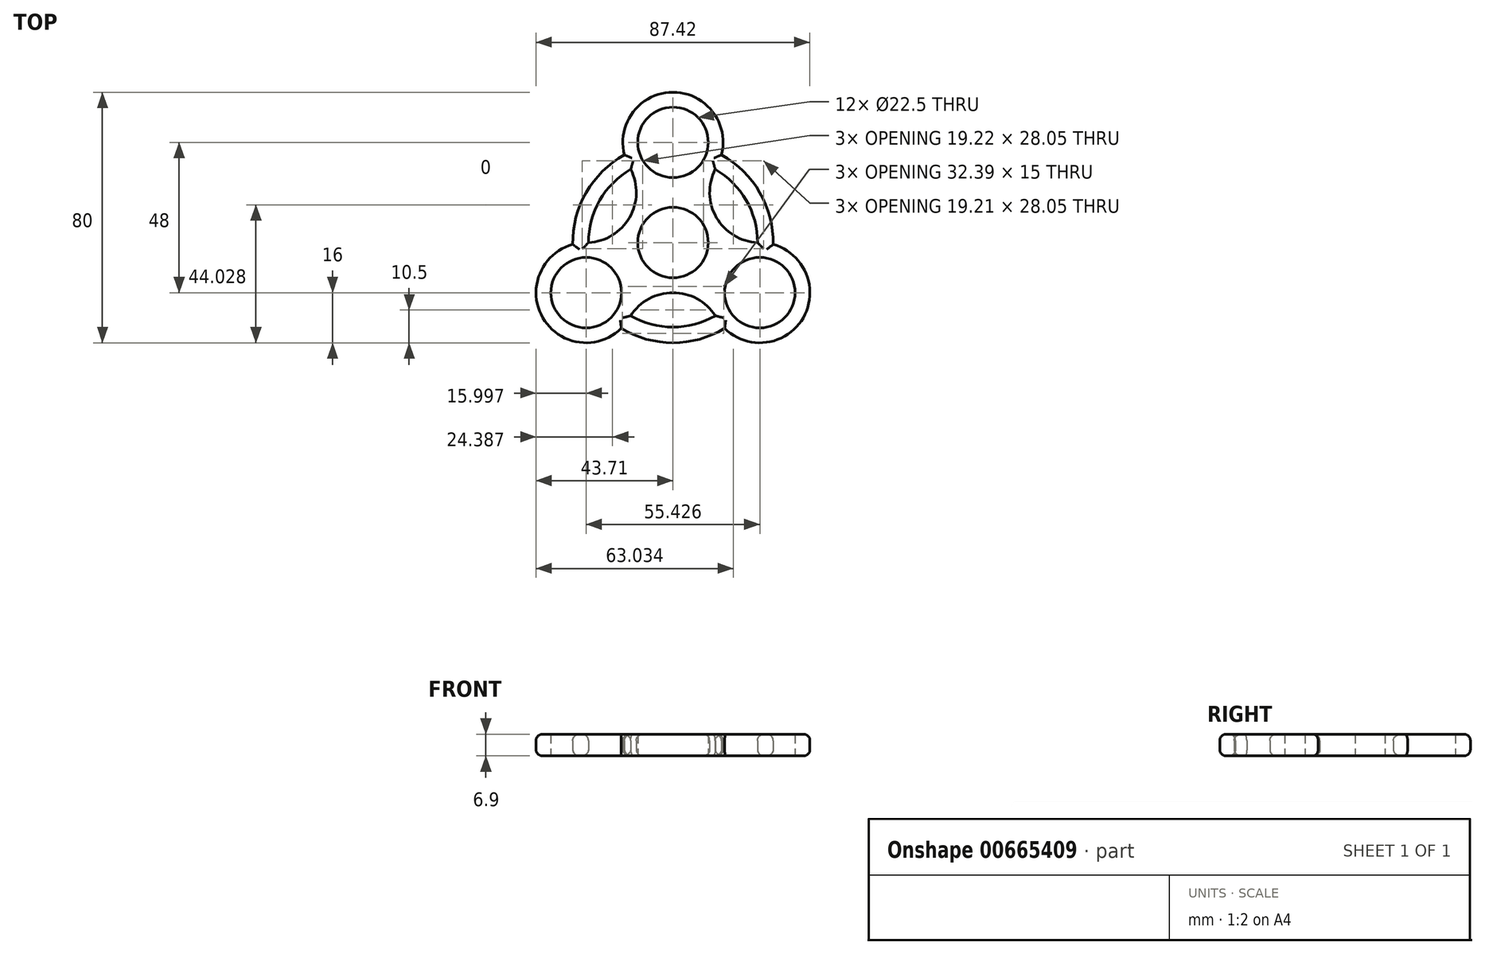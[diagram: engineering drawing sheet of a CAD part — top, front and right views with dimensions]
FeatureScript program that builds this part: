
annotation { "Feature Type Name" : "Feature", "Feature Type Description" : "" }
export const myFeature = defineFeature(function(context is Context, id is Id, definition is map)
    precondition{}
    {
        {
            var Q0;
            Q0=qCreatedBy(makeId("Top.planeOp"),FACE);
            var sketch = newSketch(context, id + "F0", { "sketchPlane" : qUnion([Q0])});
            skCircle(sketch, "E0.cCircle", {"center": v(0, 0) * mm, "radius": 32 * mm});
            skLineSegment(sketch, "E0.0", {"start": v(55.43, -32) * mm, "end": v(-55.43, -32) * mm, "construction": true});
            skLineSegment(sketch, "E0.1", {"start": v(-55.43, -32) * mm, "end": v(0, 64) * mm, "construction": true});
            skLineSegment(sketch, "E0.2", {"start": v(0, 64) * mm, "end": v(55.43, -32) * mm, "construction": true});
            skPoint(sketch, "E0.0.midPoint", {"position": v(0, -32) * mm});
            skCircle(sketch, "E1.cCircle", {"center": v(0, 0) * mm, "radius": 27 * mm});
            skLineSegment(sketch, "E1.0", {"start": v(46.77, -27) * mm, "end": v(-46.77, -27) * mm, "construction": true});
            skLineSegment(sketch, "E1.1", {"start": v(-46.77, -27) * mm, "end": v(0, 54) * mm, "construction": true});
            skLineSegment(sketch, "E1.2", {"start": v(0, 54) * mm, "end": v(46.77, -27) * mm, "construction": true});
            skPoint(sketch, "E1.0.midPoint", {"position": v(0, -27) * mm});
            skCircle(sketch, "E2.cCircle", {"center": v(0, 0) * mm, "radius": 16 * mm, "construction": true});
            skLineSegment(sketch, "E2.0", {"start": v(27.71, -16) * mm, "end": v(-27.71, -16) * mm, "construction": true});
            skLineSegment(sketch, "E2.1", {"start": v(-27.71, -16) * mm, "end": v(0, 32) * mm, "construction": true});
            skLineSegment(sketch, "E2.2", {"start": v(0, 32) * mm, "end": v(27.71, -16) * mm, "construction": true});
            skPoint(sketch, "E2.0.midPoint", {"position": v(0, -16) * mm});
            skCircle(sketch, "E3", {"center": v(-27.71, -16) * mm, "radius": 11.25 * mm});
            skCircle(sketch, "E4", {"center": v(27.71, -16) * mm, "radius": 11.25 * mm});
            skCircle(sketch, "E5", {"center": v(0, 32) * mm, "radius": 11.25 * mm});
            skCircle(sketch, "E6", {"center": v(-27.71, -16) * mm, "radius": 16 * mm});
            skCircle(sketch, "E7", {"center": v(27.71, -16) * mm, "radius": 16 * mm});
            skCircle(sketch, "E8", {"center": v(0, 32) * mm, "radius": 16 * mm});
            skArc(sketch, "E9", {"start": v(-27, -0.02) * mm, "mid": v(-13.86, 8) * mm, "end": v(-13.49, 23.4) * mm});
            skArc(sketch, "E10", {"start": v(13.49, 23.4) * mm, "mid": v(13.86, 8) * mm, "end": v(27, -0.02) * mm});
            skArc(sketch, "E11", {"start": v(13.51, -23.37) * mm, "mid": v(0, -16) * mm, "end": v(-13.51, -23.37) * mm});
            skCircle(sketch, "E12", {"center": v(0, 0) * mm, "radius": 11.25 * mm});
            skSolve(sketch);
        }
        {
            var Q0;
            Q0=makeQuery(id+"F0.imprint","IMPRINT",FACE,{"disambiguationData":[TD([[makeQuery(id+"F0.imprint","IMPRINT",EDGE,{"derivedFrom":sQuery(id+"F0.wireOp",EDGE,"E3")}),-1.0]])]});
            var Q1;
            {var subQ0=sQuery(id+"F0.wireOp",EDGE,"E9");Q1=makeQuery(id+"F0.imprint","IMPRINT",FACE,{"disambiguationData":[TD([[makeQuery(id+"F0.imprint","IMPRINT",EDGE,{"derivedFrom":subQ0}),-1.0]])]});}
            var Q2;
            Q2=makeQuery(id+"F0.imprint","IMPRINT",FACE,{"disambiguationData":[TD([[makeQuery(id+"F0.imprint","IMPRINT",EDGE,{"derivedFrom":sQuery(id+"F0.wireOp",EDGE,"E4")}),-1.0]])]});
            var Q3;
            Q3=makeQuery(id+"F0.imprint","IMPRINT",FACE,{"disambiguationData":[TD([[makeQuery(id+"F0.imprint","IMPRINT",EDGE,{"derivedFrom":sQuery(id+"F0.wireOp",EDGE,"E5")}),-1.0]])]});
            var Q4;
            {var subQ0=sQuery(id+"F0.wireOp",EDGE,"E8");var subQ1=sQuery(id+"F0.wireOp",EDGE,"E0.cCircle");var subQ2=makeQuery(id+"F0.imprint","INTERSECT",VERTEX,{"disambiguationData":[OD(1.0)],"derivedFrom":[subQ1,subQ0]});Q4=makeQuery(id+"F0.imprint","IMPRINT",FACE,{"disambiguationData":[TD([[makeQuery(id+"F0.imprint","IMPRINT",EDGE,{"disambiguationData":[TD([[subQ2,-1.0]])],"derivedFrom":subQ1}),1.0]])]});}
            var Q5;
            {var subQ0=sQuery(id+"F0.wireOp",EDGE,"E8");var subQ1=sQuery(id+"F0.wireOp",EDGE,"E0.cCircle");var subQ2=makeQuery(id+"F0.imprint","INTERSECT",VERTEX,{"disambiguationData":[OD(0.0)],"derivedFrom":[subQ1,subQ0]});Q5=makeQuery(id+"F0.imprint","IMPRINT",FACE,{"disambiguationData":[TD([[makeQuery(id+"F0.imprint","IMPRINT",EDGE,{"disambiguationData":[TD([[subQ2,1.0]])],"derivedFrom":subQ1}),1.0]])]});}
            var Q6;
            {var subQ0=sQuery(id+"F0.wireOp",EDGE,"E6");var subQ1=sQuery(id+"F0.wireOp",EDGE,"E0.cCircle");var subQ2=makeQuery(id+"F0.imprint","INTERSECT",VERTEX,{"disambiguationData":[OD(1.0)],"derivedFrom":[subQ1,subQ0]});Q6=makeQuery(id+"F0.imprint","IMPRINT",FACE,{"disambiguationData":[TD([[makeQuery(id+"F0.imprint","IMPRINT",EDGE,{"disambiguationData":[TD([[subQ2,-1.0]])],"derivedFrom":subQ1}),1.0]])]});}
            extrude(context, id + "F1", {"entities" : qUnion([Q0, Q1, Q2, Q3, Q4, Q5, Q6]), "depth" : 6.9 * mm, "offsetDistance" : 25 * mm});
        }
        {
            var Q0;
            Q0=makeQuery(id+"F1.opExtrude","CAP_EDGE",EDGE,{"disambiguationData":[OSD([sQuery(id+"F0.wireOp",EDGE,"E9")])],"isStart":true});
            var Q1;
            Q1=makeQuery(id+"F1.opExtrude","CAP_EDGE",EDGE,{"disambiguationData":[OSD([sQuery(id+"F0.wireOp",EDGE,"E9")])],"isStart":false});
            var Q2;
            Q2=makeQuery(id+"F1.opExtrude","CAP_EDGE",EDGE,{"disambiguationData":[OSD([sQuery(id+"F0.wireOp",EDGE,"E8")])],"isStart":true});
            var Q3;
            Q3=makeQuery(id+"F1.opExtrude","CAP_EDGE",EDGE,{"disambiguationData":[OSD([sQuery(id+"F0.wireOp",EDGE,"E8")])],"isStart":false});
            var Q4;
            Q4=makeQuery(id+"F1.opExtrude","CAP_EDGE",EDGE,{"disambiguationData":[OSD([sQuery(id+"F0.wireOp",EDGE,"E6")])],"isStart":true});
            var Q5;
            Q5=makeQuery(id+"F1.opExtrude","CAP_EDGE",EDGE,{"disambiguationData":[OSD([sQuery(id+"F0.wireOp",EDGE,"E6")])],"isStart":false});
            var Q6;
            Q6=makeQuery(id+"F1.opExtrude","CAP_EDGE",EDGE,{"disambiguationData":[OSD([sQuery(id+"F0.wireOp",EDGE,"E11")])],"isStart":true});
            var Q7;
            Q7=makeQuery(id+"F1.opExtrude","CAP_EDGE",EDGE,{"disambiguationData":[OSD([sQuery(id+"F0.wireOp",EDGE,"E11")])],"isStart":false});
            var Q8;
            Q8=makeQuery(id+"F1.opExtrude","CAP_EDGE",EDGE,{"disambiguationData":[OSD([sQuery(id+"F0.wireOp",EDGE,"E7")])],"isStart":true});
            var Q9;
            Q9=makeQuery(id+"F1.opExtrude","CAP_EDGE",EDGE,{"disambiguationData":[OSD([sQuery(id+"F0.wireOp",EDGE,"E7")])],"isStart":false});
            var Q10;
            Q10=makeQuery(id+"F1.opExtrude","CAP_EDGE",EDGE,{"disambiguationData":[OSD([sQuery(id+"F0.wireOp",EDGE,"E10")])],"isStart":true});
            var Q11;
            Q11=makeQuery(id+"F1.opExtrude","CAP_EDGE",EDGE,{"disambiguationData":[OSD([sQuery(id+"F0.wireOp",EDGE,"E10")])],"isStart":false});
            fillet(context, id + "F2", {"entities" : qUnion([Q0, Q1, Q2, Q3, Q4, Q5, Q6, Q7, Q8, Q9, Q10, Q11]), "radius" : 2 * mm, "tangentPropagation" : true, "allowEdgeOverflow" : false});
        }
        {
            var Q0;
            {var subQ0=sQuery(id+"F0.wireOp",EDGE,"E0.cCircle");Q0=makeQuery(id+"F1.opExtrude","CAP_EDGE",EDGE,{"disambiguationData":[OSD([subQ0]),TDD([makeQuery(id+"F0.imprint","IMPRINT",EDGE,{"disambiguationData":[TD([[makeQuery(id+"F0.imprint","INTERSECT",VERTEX,{"disambiguationData":[OD(0.0)],"derivedFrom":[subQ0,sQuery(id+"F0.wireOp",EDGE,"E8")]}),1.0]])],"derivedFrom":subQ0})])],"isStart":true});}
            var Q1;
            {var subQ0=sQuery(id+"F0.wireOp",EDGE,"E0.cCircle");Q1=makeQuery(id+"F1.opExtrude","CAP_EDGE",EDGE,{"disambiguationData":[OSD([subQ0]),TDD([makeQuery(id+"F0.imprint","IMPRINT",EDGE,{"disambiguationData":[TD([[makeQuery(id+"F0.imprint","INTERSECT",VERTEX,{"disambiguationData":[OD(0.0)],"derivedFrom":[subQ0,sQuery(id+"F0.wireOp",EDGE,"E8")]}),1.0]])],"derivedFrom":subQ0})])],"isStart":false});}
            var Q2;
            {var subQ0=sQuery(id+"F0.wireOp",EDGE,"E9");var subQ1=sQuery(id+"F0.wireOp",EDGE,"E1.cCircle");Q2=makeQuery(id+"F1.opExtrude","CAP_EDGE",EDGE,{"disambiguationData":[OSD([subQ1]),TDD([makeQuery(id+"F0.imprint","IMPRINT",EDGE,{"disambiguationData":[TD([[makeQuery(id+"F0.imprint","INTERSECT",VERTEX,{"derivedFrom":[subQ1,sQuery(id+"F0.wireOp",EDGE,"E6"),subQ0]}),1.0]])],"derivedFrom":subQ1})])],"isStart":false});}
            var Q3;
            {var subQ0=sQuery(id+"F0.wireOp",EDGE,"E9");var subQ1=sQuery(id+"F0.wireOp",EDGE,"E1.cCircle");Q3=makeQuery(id+"F1.opExtrude","CAP_EDGE",EDGE,{"disambiguationData":[OSD([subQ1]),TDD([makeQuery(id+"F0.imprint","IMPRINT",EDGE,{"disambiguationData":[TD([[makeQuery(id+"F0.imprint","INTERSECT",VERTEX,{"derivedFrom":[subQ1,sQuery(id+"F0.wireOp",EDGE,"E6"),subQ0]}),1.0]])],"derivedFrom":subQ1})])],"isStart":true});}
            var Q4;
            {var subQ0=sQuery(id+"F0.wireOp",EDGE,"E0.cCircle");Q4=makeQuery(id+"F1.opExtrude","CAP_EDGE",EDGE,{"disambiguationData":[OSD([subQ0]),TDD([makeQuery(id+"F0.imprint","IMPRINT",EDGE,{"disambiguationData":[TD([[makeQuery(id+"F0.imprint","INTERSECT",VERTEX,{"disambiguationData":[OD(1.0)],"derivedFrom":[subQ0,sQuery(id+"F0.wireOp",EDGE,"E8")]}),-1.0]])],"derivedFrom":subQ0})])],"isStart":false});}
            var Q5;
            {var subQ0=sQuery(id+"F0.wireOp",EDGE,"E11");var subQ1=sQuery(id+"F0.wireOp",EDGE,"E1.cCircle");Q5=makeQuery(id+"F1.opExtrude","CAP_EDGE",EDGE,{"disambiguationData":[OSD([subQ1]),TDD([makeQuery(id+"F0.imprint","IMPRINT",EDGE,{"disambiguationData":[TD([[makeQuery(id+"F0.imprint","INTERSECT",VERTEX,{"derivedFrom":[subQ1,sQuery(id+"F0.wireOp",EDGE,"E7"),subQ0]}),1.0]])],"derivedFrom":subQ1})])],"isStart":true});}
            var Q6;
            {var subQ0=sQuery(id+"F0.wireOp",EDGE,"E11");var subQ1=sQuery(id+"F0.wireOp",EDGE,"E1.cCircle");Q6=makeQuery(id+"F1.opExtrude","CAP_EDGE",EDGE,{"disambiguationData":[OSD([subQ1]),TDD([makeQuery(id+"F0.imprint","IMPRINT",EDGE,{"disambiguationData":[TD([[makeQuery(id+"F0.imprint","INTERSECT",VERTEX,{"derivedFrom":[subQ1,sQuery(id+"F0.wireOp",EDGE,"E7"),subQ0]}),1.0]])],"derivedFrom":subQ1})])],"isStart":false});}
            var Q7;
            {var subQ0=sQuery(id+"F0.wireOp",EDGE,"E0.cCircle");Q7=makeQuery(id+"F1.opExtrude","CAP_EDGE",EDGE,{"disambiguationData":[OSD([subQ0]),TDD([makeQuery(id+"F0.imprint","IMPRINT",EDGE,{"disambiguationData":[TD([[makeQuery(id+"F0.imprint","INTERSECT",VERTEX,{"disambiguationData":[OD(1.0)],"derivedFrom":[subQ0,sQuery(id+"F0.wireOp",EDGE,"E6")]}),-1.0]])],"derivedFrom":subQ0})])],"isStart":false});}
            var Q8;
            {var subQ0=sQuery(id+"F0.wireOp",EDGE,"E0.cCircle");Q8=makeQuery(id+"F1.opExtrude","CAP_EDGE",EDGE,{"disambiguationData":[OSD([subQ0]),TDD([makeQuery(id+"F0.imprint","IMPRINT",EDGE,{"disambiguationData":[TD([[makeQuery(id+"F0.imprint","INTERSECT",VERTEX,{"disambiguationData":[OD(1.0)],"derivedFrom":[subQ0,sQuery(id+"F0.wireOp",EDGE,"E6")]}),-1.0]])],"derivedFrom":subQ0})])],"isStart":true});}
            var Q9;
            {var subQ0=sQuery(id+"F0.wireOp",EDGE,"E0.cCircle");Q9=makeQuery(id+"F1.opExtrude","CAP_EDGE",EDGE,{"disambiguationData":[OSD([subQ0]),TDD([makeQuery(id+"F0.imprint","IMPRINT",EDGE,{"disambiguationData":[TD([[makeQuery(id+"F0.imprint","INTERSECT",VERTEX,{"disambiguationData":[OD(1.0)],"derivedFrom":[subQ0,sQuery(id+"F0.wireOp",EDGE,"E8")]}),-1.0]])],"derivedFrom":subQ0})])],"isStart":true});}
            var Q10;
            {var subQ0=sQuery(id+"F0.wireOp",EDGE,"E10");var subQ1=sQuery(id+"F0.wireOp",EDGE,"E1.cCircle");Q10=makeQuery(id+"F1.opExtrude","CAP_EDGE",EDGE,{"disambiguationData":[OSD([subQ1]),TDD([makeQuery(id+"F0.imprint","IMPRINT",EDGE,{"disambiguationData":[TD([[makeQuery(id+"F0.imprint","INTERSECT",VERTEX,{"derivedFrom":[subQ1,sQuery(id+"F0.wireOp",EDGE,"E8"),subQ0]}),1.0]])],"derivedFrom":subQ1})])],"isStart":false});}
            var Q11;
            {var subQ0=sQuery(id+"F0.wireOp",EDGE,"E10");var subQ1=sQuery(id+"F0.wireOp",EDGE,"E1.cCircle");Q11=makeQuery(id+"F1.opExtrude","CAP_EDGE",EDGE,{"disambiguationData":[OSD([subQ1]),TDD([makeQuery(id+"F0.imprint","IMPRINT",EDGE,{"disambiguationData":[TD([[makeQuery(id+"F0.imprint","INTERSECT",VERTEX,{"derivedFrom":[subQ1,sQuery(id+"F0.wireOp",EDGE,"E8"),subQ0]}),1.0]])],"derivedFrom":subQ1})])],"isStart":true});}
            fillet(context, id + "F3", {"entities" : qUnion([Q0, Q1, Q2, Q3, Q4, Q5, Q6, Q7, Q8, Q9, Q10, Q11]), "radius" : 2 * mm, "tangentPropagation" : true, "allowEdgeOverflow" : false});
        }
    });
